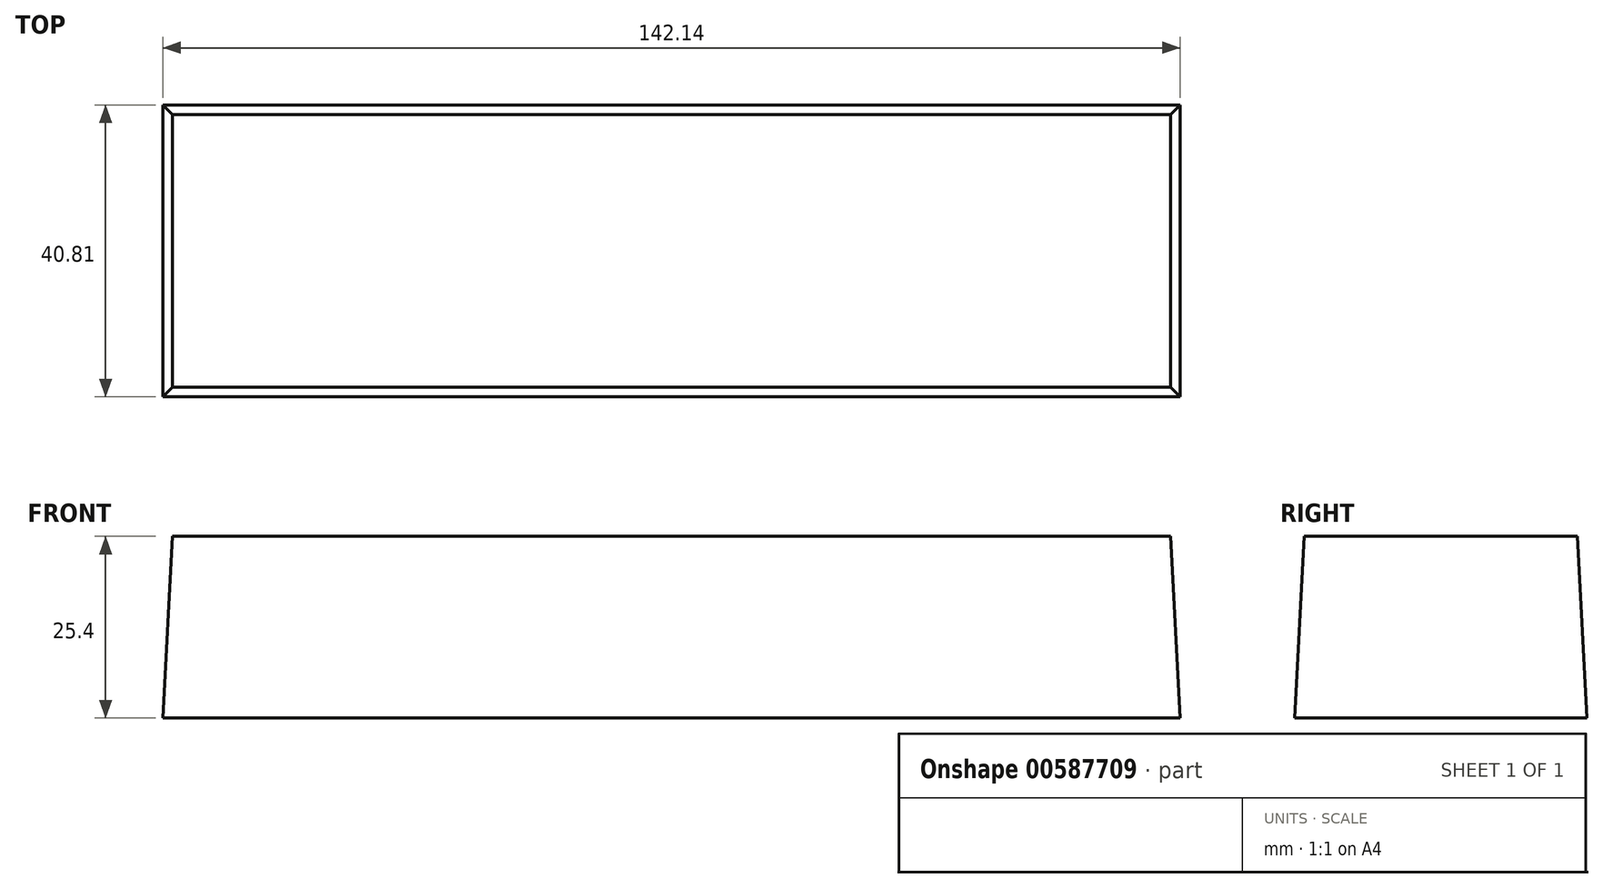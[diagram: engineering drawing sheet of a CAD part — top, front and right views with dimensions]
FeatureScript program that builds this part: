
annotation { "Feature Type Name" : "Feature", "Feature Type Description" : "" }
export const myFeature = defineFeature(function(context is Context, id is Id, definition is map)
    precondition{}
    {
        {
            var Q0;
            Q0=qCreatedBy(makeId("Top.planeOp"),FACE);
            var sketch = newSketch(context, id + "F0", { "sketchPlane" : qUnion([Q0])});
            skLineSegment(sketch, "E0.bottom", {"start": v(0, 0) * mm, "end": v(139.48, 0) * mm});
            skLineSegment(sketch, "E0.top", {"start": v(0, 38.15) * mm, "end": v(139.48, 38.15) * mm});
            skLineSegment(sketch, "E0.left", {"start": v(0, 0) * mm, "end": v(0, 38.15) * mm});
            skLineSegment(sketch, "E0.right", {"start": v(139.48, 0) * mm, "end": v(139.48, 38.15) * mm});
            skSolve(sketch);
        }
        {
            var Q0;
            Q0=makeQuery(id+"F0.imprint","IMPRINT",FACE,{"disambiguationData":[TD([[makeQuery(id+"F0.imprint","IMPRINT",EDGE,{"derivedFrom":sQuery(id+"F0.wireOp",EDGE,"E0.bottom")}),1.0]])]});
            extrude(context, id + "F1", {"entities" : qUnion([Q0]), "oppositeDirection" : true, "depth" : 25.4 * mm, "offsetDistance" : 25.4 * mm, "hasDraft" : true, "draftAngle" : 3 * degree});
        }
        {
            var Q0;
            Q0=makeQuery(id+"F1.opExtrude","CAP_FACE",FACE,{"disambiguationData":[OSD([sQuery(id+"F0.wireOp",EDGE,"E0.bottom"),sQuery(id+"F0.wireOp",EDGE,"E0.top"),sQuery(id+"F0.wireOp",EDGE,"E0.left"),sQuery(id+"F0.wireOp",EDGE,"E0.right")])],"isStart":true});
            var sketch = newSketch(context, id + "F2", { "sketchPlane" : qUnion([Q0])});
            skSolve(sketch);
        }
    });
